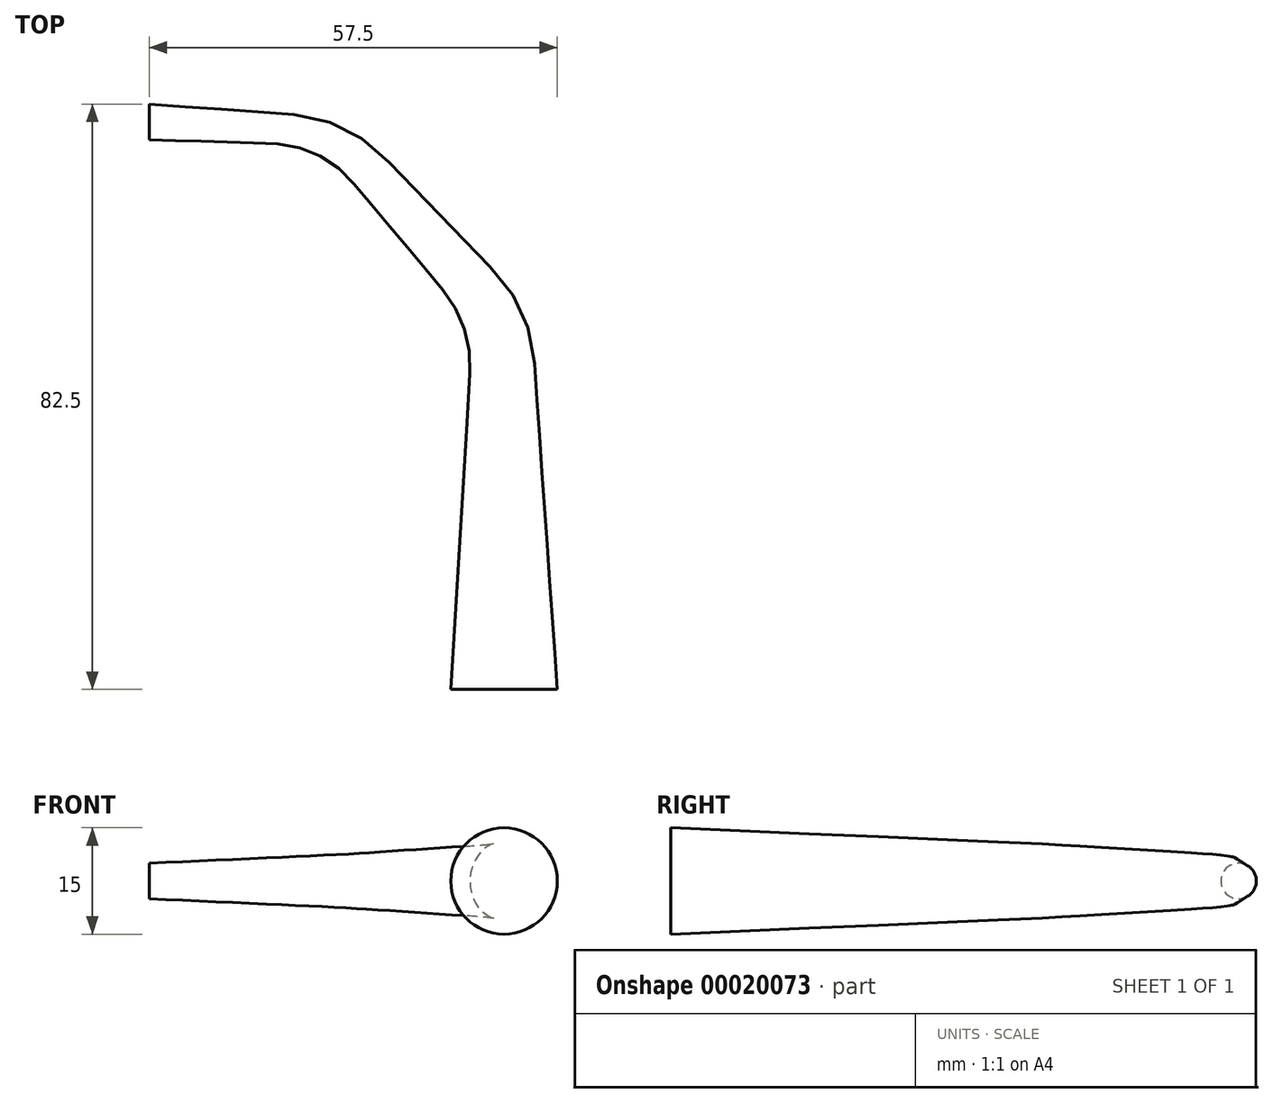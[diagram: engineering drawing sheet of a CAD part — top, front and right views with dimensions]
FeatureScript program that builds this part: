
annotation { "Feature Type Name" : "Feature", "Feature Type Description" : "" }
export const myFeature = defineFeature(function(context is Context, id is Id, definition is map)
    precondition{}
    {
        {
            var Q0;
            Q0=qCreatedBy(makeId("Front.planeOp"),FACE);
            var sketch = newSketch(context, id + "F0", { "sketchPlane" : qUnion([Q0])});
            skCircle(sketch, "E0", {"center": v(50, 0) * mm, "radius": 7.5 * mm});
            skPoint(sketch, "E1", {"position": v(57.5, 0) * mm});
            skPoint(sketch, "E2", {"position": v(42.5, 0) * mm});
            skSolve(sketch);
        }
        {
            var Q0;
            Q0=qCreatedBy(makeId("Right.planeOp"),FACE);
            var sketch = newSketch(context, id + "F1", { "sketchPlane" : qUnion([Q0])});
            skCircle(sketch, "E3", {"center": v(80, 0) * mm, "radius": 2.5 * mm});
            skPoint(sketch, "E4", {"position": v(82.5, 0) * mm});
            skPoint(sketch, "E5", {"position": v(77.5, 0) * mm});
            skSolve(sketch);
        }
        {
            var Q0;
            Q0=qCreatedBy(makeId("Top.planeOp"),FACE);
            var sketch = newSketch(context, id + "F2", { "sketchPlane" : qUnion([Q0])});
            skLineSegment(sketch, "E6", {"start": v(57.5, 0) * mm, "end": v(54.26, 46.38) * mm});
            skLineSegment(sketch, "E7", {"start": v(48.7, 58.88) * mm, "end": v(33.09, 75.04) * mm});
            skLineSegment(sketch, "E8", {"start": v(20.1, 81.1) * mm, "end": v(0, 82.5) * mm});
            skPoint(sketch, "E9.visualSharp", {"position": v(27.75, 80.56) * mm});
            skArc(sketch, "E9.filletArc", {"start": v(33.09, 75.04) * mm, "mid": v(27.15, 79.27) * mm, "end": v(20.1, 81.1) * mm});
            skPoint(sketch, "E10.visualSharp", {"position": v(53.75, 53.64) * mm});
            skArc(sketch, "E10.filletArc", {"start": v(54.26, 46.38) * mm, "mid": v(52.58, 53.12) * mm, "end": v(48.7, 58.88) * mm});
            skLineSegment(sketch, "E11", {"start": v(0, 82.5) * mm, "end": v(57.5, 82.5) * mm, "construction": true});
            skLineSegment(sketch, "E12", {"start": v(57.5, 0) * mm, "end": v(57.5, 82.5) * mm, "construction": true});
            skSolve(sketch);
        }
        {
            var Q0;
            Q0=makeQuery(id+"F0.imprint","IMPRINT",FACE,{"disambiguationData":[TD([[makeQuery(id+"F0.imprint","IMPRINT",EDGE,{"derivedFrom":sQuery(id+"F0.wireOp",EDGE,"E0")}),1.0]])]});
            var Q1;
            Q1=makeQuery(id+"F1.imprint","IMPRINT",FACE,{"disambiguationData":[TD([[makeQuery(id+"F1.imprint","IMPRINT",EDGE,{"derivedFrom":sQuery(id+"F1.wireOp",EDGE,"E3")}),1.0]])]});
            var Q2;
            Q2 = qConstructionFilter(qBodyType(qCreatedBy(id + "F2" ,EDGE), BodyType.WIRE), ConstructionObject.NO);
            var Q3;
            Q3=sQuery(id+"F0.wireOp",VERTEX,"E1");
            var Q4;
            Q4=sQuery(id+"F1.wireOp",VERTEX,"E4");
            loft(context, id + "F3", {"addGuides" : true, "sheetProfilesArray" : [{ "sheetProfileEntities" : qUnion([Q0]) }, { "sheetProfileEntities" : qUnion([Q1]) }], "guidesArray" : [{ "guideEntities" : qUnion([Q2]), "guideDerivativeType" : LoftGuideDerivativeType.DEFAULT, "guideDerivativeMagnitude" : 1 }], "connections" : [{ "connectionEntities" : qUnion([Q3, Q4]), "connectionEdgeQueries" : qUnion([]), "connectionEdgeParameters" : [] }]});
        }
    });
